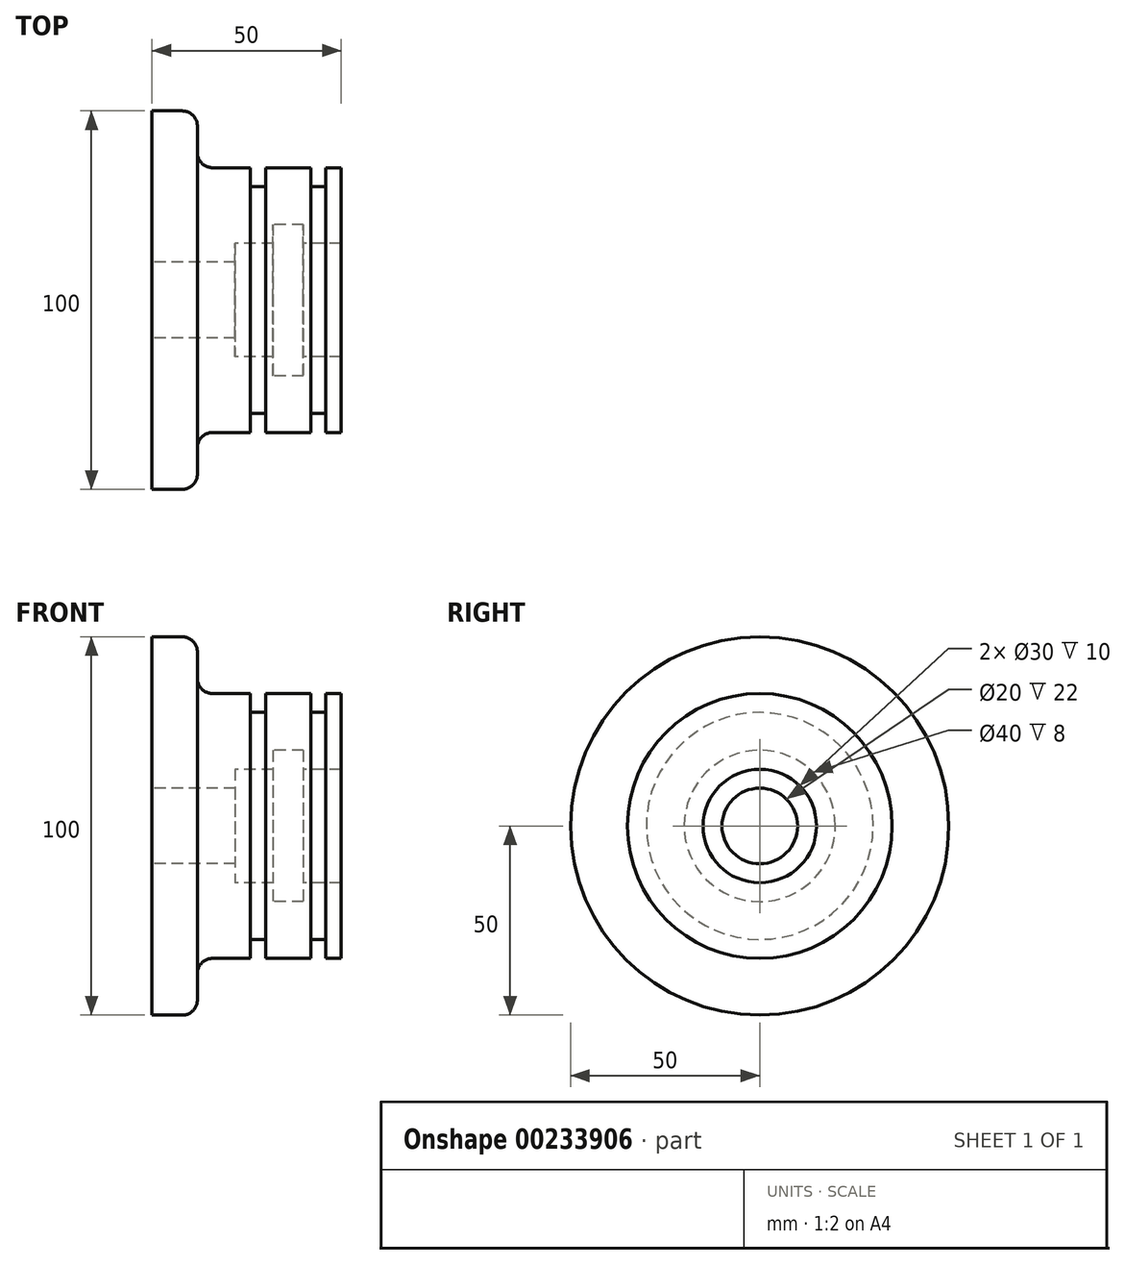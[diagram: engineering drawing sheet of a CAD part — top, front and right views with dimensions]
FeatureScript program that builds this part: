
annotation { "Feature Type Name" : "Feature", "Feature Type Description" : "" }
export const myFeature = defineFeature(function(context is Context, id is Id, definition is map)
    precondition{}
    {
        {
            var Q0;
            Q0=qCreatedBy(makeId("Front.planeOp"),FACE);
            var sketch = newSketch(context, id + "F0", { "sketchPlane" : qUnion([Q0])});
            skLineSegment(sketch, "E0", {"start": v(-85.4, 0) * mm, "end": v(84.96, 0) * mm});
            skLineSegment(sketch, "E1", {"start": v(-54.9, 0) * mm, "end": v(-54.9, 50) * mm});
            skLineSegment(sketch, "E2", {"start": v(-54.9, 50) * mm, "end": v(-46.9, 50) * mm});
            skLineSegment(sketch, "E3", {"start": v(-42.9, 46) * mm, "end": v(-42.9, 39) * mm});
            skLineSegment(sketch, "E4", {"start": v(-38.9, 35) * mm, "end": v(-28.9, 35) * mm});
            skLineSegment(sketch, "E5", {"start": v(-28.9, 35) * mm, "end": v(-28.9, 30) * mm});
            skLineSegment(sketch, "E6", {"start": v(-28.9, 30) * mm, "end": v(-24.9, 30) * mm});
            skLineSegment(sketch, "E7", {"start": v(-24.9, 30) * mm, "end": v(-24.9, 35) * mm});
            skLineSegment(sketch, "E8", {"start": v(-24.9, 35) * mm, "end": v(-12.9, 35) * mm});
            skLineSegment(sketch, "E9", {"start": v(-12.9, 35) * mm, "end": v(-12.9, 30) * mm});
            skLineSegment(sketch, "E10", {"start": v(-12.9, 30) * mm, "end": v(-8.9, 30) * mm});
            skLineSegment(sketch, "E11", {"start": v(-8.9, 30) * mm, "end": v(-8.9, 35) * mm});
            skLineSegment(sketch, "E12", {"start": v(-8.9, 35) * mm, "end": v(-4.9, 35) * mm});
            skLineSegment(sketch, "E13", {"start": v(-4.9, 35) * mm, "end": v(-4.9, 0) * mm});
            skLineSegment(sketch, "E14", {"start": v(-54.9, 10) * mm, "end": v(-32.9, 10) * mm});
            skLineSegment(sketch, "E15", {"start": v(-32.9, 10) * mm, "end": v(-32.9, 0) * mm});
            skLineSegment(sketch, "E16", {"start": v(-32.9, 0) * mm, "end": v(-54.9, 0) * mm});
            skLineSegment(sketch, "E17", {"start": v(-32.9, 10) * mm, "end": v(-32.9, 15) * mm});
            skLineSegment(sketch, "E18", {"start": v(-32.9, 15) * mm, "end": v(-22.9, 15) * mm});
            skLineSegment(sketch, "E19", {"start": v(-22.9, 15) * mm, "end": v(-22.9, 0) * mm});
            skLineSegment(sketch, "E20", {"start": v(-22.9, 0) * mm, "end": v(-32.9, 0) * mm});
            skLineSegment(sketch, "E21", {"start": v(-22.9, 15) * mm, "end": v(-22.9, 20) * mm});
            skLineSegment(sketch, "E22", {"start": v(-22.9, 20) * mm, "end": v(-14.9, 20) * mm});
            skLineSegment(sketch, "E23", {"start": v(-14.9, 20) * mm, "end": v(-14.9, 0) * mm});
            skLineSegment(sketch, "E24", {"start": v(-14.9, 0) * mm, "end": v(-22.9, 0) * mm});
            skLineSegment(sketch, "E25", {"start": v(-14.9, 15) * mm, "end": v(-4.9, 15) * mm});
            skLineSegment(sketch, "E26", {"start": v(-14.9, 0) * mm, "end": v(-4.9, 0) * mm});
            skPoint(sketch, "E27.visualSharp", {"position": v(-42.9, 50) * mm});
            skArc(sketch, "E27.filletArc", {"start": v(-42.9, 46) * mm, "mid": v(-44.06, 48.83) * mm, "end": v(-46.9, 50) * mm});
            skPoint(sketch, "E28.visualSharp", {"position": v(-42.9, 35) * mm});
            skArc(sketch, "E28.filletArc", {"start": v(-42.9, 39) * mm, "mid": v(-41.72, 36.17) * mm, "end": v(-38.9, 35) * mm});
            skSolve(sketch);
        }
        {
            var Q0;
            {var subQ1=sQuery(id+"F0.wireOp",EDGE,"E2");Q0=makeQuery(id+"F0.imprint","IMPRINT",FACE,{"disambiguationData":[TD([[makeQuery(id+"F0.imprint","IMPRINT",EDGE,{"derivedFrom":subQ1}),-1.0]])]});}
            var Q1;
            Q1=sQuery(id+"F0.wireOp",EDGE,"E0");
            revolve(context, id + "F1", {"entities" : qUnion([Q0]), "axis" : qUnion([Q1]), "revolveType" : RevolveType.FULL});
        }
    });
